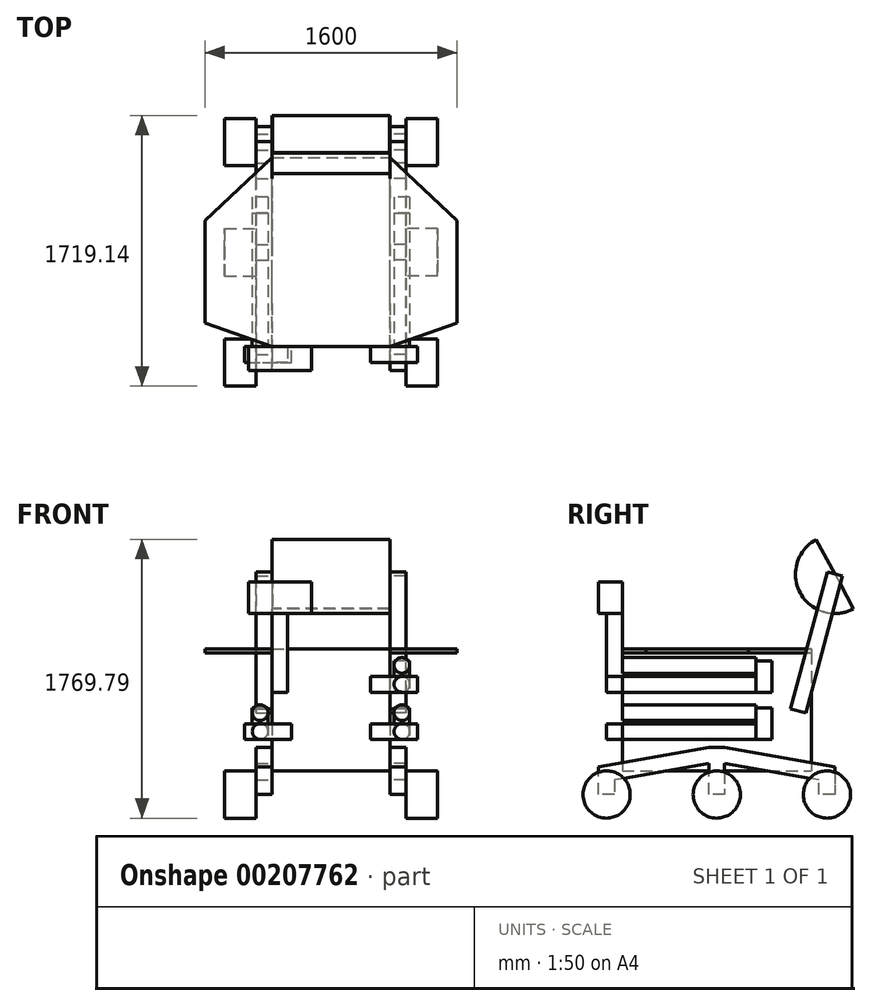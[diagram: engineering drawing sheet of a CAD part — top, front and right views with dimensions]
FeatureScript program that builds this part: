
annotation { "Feature Type Name" : "Feature", "Feature Type Description" : "" }
export const myFeature = defineFeature(function(context is Context, id is Id, definition is map)
    precondition{}
    {
        {
            var Q0;
            Q0=qCreatedBy(makeId("Front.planeOp"),FACE);
            var sketch = newSketch(context, id + "F0", { "sketchPlane" : qUnion([Q0])});
            skLineSegment(sketch, "E0.bottom", {"start": v(-375, 900) * mm, "end": v(375, 900) * mm});
            skLineSegment(sketch, "E0.top", {"start": v(-375, 150) * mm, "end": v(375, 150) * mm});
            skLineSegment(sketch, "E0.left", {"start": v(-375, 900) * mm, "end": v(-375, 150) * mm});
            skLineSegment(sketch, "E0.right", {"start": v(375, 900) * mm, "end": v(375, 150) * mm});
            skSolve(sketch);
        }
        {
            var Q0;
            Q0=makeQuery(id+"F0.imprint","IMPRINT",FACE,{"disambiguationData":[TD([[makeQuery(id+"F0.imprint","IMPRINT",EDGE,{"derivedFrom":sQuery(id+"F0.wireOp",EDGE,"E0.bottom")}),-1.0]])]});
            extrude(context, id + "F1", {"entities" : qUnion([Q0]), "endBound" : BoundingType.SYMMETRIC, "depth" : 1200 * mm, "offsetDistance" : 25 * mm});
        }
        {
            var Q0;
            Q0=makeQuery(id+"F1.opExtrude","SWEPT_FACE",FACE,{"disambiguationData":[OSD([sQuery(id+"F0.wireOp",EDGE,"E0.bottom")])]});
            var sketch = newSketch(context, id + "F2", { "sketchPlane" : qUnion([Q0])});
            skLineSegment(sketch, "E1", {"start": v(-375, -600) * mm, "end": v(-800, -450) * mm});
            skLineSegment(sketch, "E2", {"start": v(-800, -450) * mm, "end": v(-800, 200) * mm});
            skLineSegment(sketch, "E3", {"start": v(-800, 200) * mm, "end": v(-375, 600) * mm});
            skLineSegment(sketch, "E4", {"start": v(-375, 600) * mm, "end": v(375, 600) * mm});
            skLineSegment(sketch, "E5", {"start": v(375, 600) * mm, "end": v(800, 200) * mm});
            skLineSegment(sketch, "E6", {"start": v(800, 200) * mm, "end": v(800, -450) * mm});
            skLineSegment(sketch, "E7", {"start": v(800, -450) * mm, "end": v(375, -600) * mm});
            skLineSegment(sketch, "E8", {"start": v(375, -600) * mm, "end": v(-375, -600) * mm});
            skSolve(sketch);
        }
        {
            var Q0;
            Q0 = qSketchRegion(id + "F2", true);
            extrude(context, id + "F3", {"entities" : qUnion([Q0]), "operationType" : NewBodyOperationType.ADD, "depth" : 25 * mm, "offsetDistance" : 25 * mm});
        }
        {
            var Q0;
            Q0=makeQuery(id+"F1.opExtrude","SWEPT_FACE",FACE,{"disambiguationData":[OSD([sQuery(id+"F0.wireOp",EDGE,"E0.left")])]});
            var sketch = newSketch(context, id + "F4", { "sketchPlane" : qUnion([Q0])});
            skLineSegment(sketch, "E9.bottom", {"start": v(600, 1150) * mm, "end": v(700, 1150) * mm});
            skLineSegment(sketch, "E9.top", {"start": v(600, 650) * mm, "end": v(700, 650) * mm});
            skLineSegment(sketch, "E9.left", {"start": v(600, 1150) * mm, "end": v(600, 650) * mm});
            skLineSegment(sketch, "E9.right", {"start": v(700, 1150) * mm, "end": v(700, 650) * mm});
            skSolve(sketch);
        }
        {
            var Q0;
            Q0 = qSketchRegion(id + "F4", true);
            extrude(context, id + "F5", {"entities" : qUnion([Q0]), "operationType" : NewBodyOperationType.ADD, "oppositeDirection" : true, "depth" : 100 * mm, "offsetDistance" : 25 * mm});
        }
        {
            var Q0;
            Q0=makeQuery(id+"F5.opExtrude","SWEPT_FACE",FACE,{"disambiguationData":[OSD([sQuery(id+"F4.wireOp",EDGE,"E9.left")])]});
            var sketch = newSketch(context, id + "F6", { "sketchPlane" : qUnion([Q0])});
            skPoint(sketch, "E10.oppositeSnap0", {"position": v(325, 1150) * mm});
            skLineSegment(sketch, "E10.bottom", {"start": v(125, 1350) * mm, "end": v(525, 1350) * mm});
            skLineSegment(sketch, "E10.top", {"start": v(125, 1150) * mm, "end": v(525, 1150) * mm});
            skLineSegment(sketch, "E10.left", {"start": v(125, 1350) * mm, "end": v(125, 1150) * mm});
            skLineSegment(sketch, "E10.right", {"start": v(525, 1350) * mm, "end": v(525, 1150) * mm});
            skSolve(sketch);
        }
        {
            var Q0;
            Q0 = qSketchRegion(id + "F6", true);
            extrude(context, id + "F7", {"entities" : qUnion([Q0]), "oppositeDirection" : true, "depth" : 150 * mm, "offsetDistance" : 25 * mm});
        }
        {
            var Q0;
            Q0=makeQuery(id+"F5.boolean.opBoolean","MERGE",FACE,{"derivedFrom":[makeQuery(id+"F1.opExtrude","SWEPT_FACE",FACE,{"disambiguationData":[OSD([sQuery(id+"F0.wireOp",EDGE,"E0.left")])]}),makeQuery(id+"F5.opExtrude","CAP_FACE",FACE,{"disambiguationData":[OSD([sQuery(id+"F4.wireOp",EDGE,"E9.bottom"),sQuery(id+"F4.wireOp",EDGE,"E9.top"),sQuery(id+"F4.wireOp",EDGE,"E9.left"),sQuery(id+"F4.wireOp",EDGE,"E9.right")])],"isStart":true})]});
            var sketch = newSketch(context, id + "F8", { "sketchPlane" : qUnion([Q0])});
            skLineSegment(sketch, "E11", {"start": v(-50, 300) * mm, "end": v(-750, 176.57) * mm});
            skLineSegment(sketch, "E12", {"start": v(-750, 176.57) * mm, "end": v(-750, 0) * mm});
            skLineSegment(sketch, "E13", {"start": v(-750, 0) * mm, "end": v(-650, 0) * mm});
            skLineSegment(sketch, "E14", {"start": v(-650, 0) * mm, "end": v(-650, 92.66) * mm});
            skLineSegment(sketch, "E15", {"start": v(-650, 92.66) * mm, "end": v(-50, 198.46) * mm});
            skLineSegment(sketch, "E16", {"start": v(-50, 198.46) * mm, "end": v(-50, 0) * mm});
            skLineSegment(sketch, "E17", {"start": v(-50, 0) * mm, "end": v(50, 0) * mm});
            skLineSegment(sketch, "E18", {"start": v(50, 0) * mm, "end": v(50, 198.46) * mm});
            skLineSegment(sketch, "E19", {"start": v(50, 198.46) * mm, "end": v(650, 92.66) * mm});
            skLineSegment(sketch, "E20", {"start": v(650, 92.66) * mm, "end": v(650, 0) * mm});
            skLineSegment(sketch, "E21", {"start": v(650, 0) * mm, "end": v(750, 0) * mm});
            skLineSegment(sketch, "E22", {"start": v(750, 0) * mm, "end": v(750, 176.57) * mm});
            skLineSegment(sketch, "E23", {"start": v(750, 176.57) * mm, "end": v(50, 300) * mm});
            skLineSegment(sketch, "E24", {"start": v(-50, 300) * mm, "end": v(50, 300) * mm});
            skSolve(sketch);
        }
        {
            var Q0;
            Q0=makeQuery(id+"F1.opExtrude","SWEPT_FACE",FACE,{"disambiguationData":[OSD([sQuery(id+"F0.wireOp",EDGE,"E0.right")])]});
            var sketch = newSketch(context, id + "F9", { "sketchPlane" : qUnion([Q0])});
            skLineSegment(sketch, "E25.0", {"start": v(-750, 0) * mm, "end": v(-750, 176.57) * mm});
            skPoint(sketch, "E26.0", {"position": v(-700, 0) * mm});
            skLineSegment(sketch, "E27.0", {"start": v(-650, 0) * mm, "end": v(-750, 0) * mm});
            skLineSegment(sketch, "E28.0", {"start": v(-650, 92.66) * mm, "end": v(-650, 0) * mm});
            skLineSegment(sketch, "E29.0", {"start": v(-50, 198.46) * mm, "end": v(-650, 92.66) * mm});
            skLineSegment(sketch, "E30.0", {"start": v(-750, 176.57) * mm, "end": v(-50, 300) * mm});
            skLineSegment(sketch, "E31.0", {"start": v(-50, 0) * mm, "end": v(-50, 198.46) * mm});
            skLineSegment(sketch, "E32.0", {"start": v(50, 0) * mm, "end": v(-50, 0) * mm});
            skLineSegment(sketch, "E33.0", {"start": v(50, 198.46) * mm, "end": v(50, 0) * mm});
            skLineSegment(sketch, "E34.0", {"start": v(50, 300) * mm, "end": v(-50, 300) * mm});
            skLineSegment(sketch, "E35.0", {"start": v(650, 92.66) * mm, "end": v(50, 198.46) * mm});
            skLineSegment(sketch, "E36.0", {"start": v(50, 300) * mm, "end": v(750, 176.57) * mm});
            skLineSegment(sketch, "E37.0", {"start": v(750, 176.57) * mm, "end": v(750, 0) * mm});
            skLineSegment(sketch, "E38.0", {"start": v(650, 0) * mm, "end": v(650, 92.66) * mm});
            skLineSegment(sketch, "E39.0", {"start": v(750, 0) * mm, "end": v(650, 0) * mm});
            skSolve(sketch);
        }
        {
            var Q0;
            Q0 = qSketchRegion(id + "F8", true);
            extrude(context, id + "F10", {"entities" : qUnion([Q0]), "operationType" : NewBodyOperationType.ADD, "depth" : 100 * mm, "offsetDistance" : 25 * mm});
        }
        {
            var Q0;
            Q0 = qSketchRegion(id + "F9", true);
            extrude(context, id + "F11", {"entities" : qUnion([Q0]), "operationType" : NewBodyOperationType.ADD, "depth" : 100 * mm, "offsetDistance" : 25 * mm});
        }
        {
            var Q0;
            Q0=makeQuery(id+"F11.opExtrude","CAP_FACE",FACE,{"disambiguationData":[OSD([sQuery(id+"F9.wireOp",EDGE,"E25.0"),sQuery(id+"F9.wireOp",EDGE,"E27.0"),sQuery(id+"F9.wireOp",EDGE,"E28.0"),sQuery(id+"F9.wireOp",EDGE,"E29.0"),sQuery(id+"F9.wireOp",EDGE,"E30.0"),sQuery(id+"F9.wireOp",EDGE,"E31.0"),sQuery(id+"F9.wireOp",EDGE,"E32.0"),sQuery(id+"F9.wireOp",EDGE,"E33.0"),sQuery(id+"F9.wireOp",EDGE,"E34.0"),sQuery(id+"F9.wireOp",EDGE,"E35.0"),sQuery(id+"F9.wireOp",EDGE,"E36.0"),sQuery(id+"F9.wireOp",EDGE,"E37.0"),sQuery(id+"F9.wireOp",EDGE,"E38.0"),sQuery(id+"F9.wireOp",EDGE,"E39.0")])],"isStart":false});
            var sketch = newSketch(context, id + "F12", { "sketchPlane" : qUnion([Q0])});
            skCircle(sketch, "E40", {"center": v(-700, 0) * mm, "radius": 150 * mm});
            skCircle(sketch, "E41", {"center": v(0, 0) * mm, "radius": 150 * mm});
            skCircle(sketch, "E42", {"center": v(700, 0) * mm, "radius": 150 * mm});
            skSolve(sketch);
        }
        {
            var Q0;
            Q0=makeQuery(id+"F10.opExtrude","CAP_FACE",FACE,{"disambiguationData":[OSD([sQuery(id+"F8.wireOp",EDGE,"E11"),sQuery(id+"F8.wireOp",EDGE,"E12"),sQuery(id+"F8.wireOp",EDGE,"E13"),sQuery(id+"F8.wireOp",EDGE,"E14"),sQuery(id+"F8.wireOp",EDGE,"E15"),sQuery(id+"F8.wireOp",EDGE,"E16"),sQuery(id+"F8.wireOp",EDGE,"E17"),sQuery(id+"F8.wireOp",EDGE,"E18"),sQuery(id+"F8.wireOp",EDGE,"E19"),sQuery(id+"F8.wireOp",EDGE,"E20"),sQuery(id+"F8.wireOp",EDGE,"E21"),sQuery(id+"F8.wireOp",EDGE,"E22"),sQuery(id+"F8.wireOp",EDGE,"E23"),sQuery(id+"F8.wireOp",EDGE,"E24")])],"isStart":false});
            var sketch = newSketch(context, id + "F13", { "sketchPlane" : qUnion([Q0])});
            skCircle(sketch, "E43.0", {"center": v(-700, 0) * mm, "radius": 150 * mm});
            skCircle(sketch, "E44.0", {"center": v(0, 0) * mm, "radius": 150 * mm});
            skCircle(sketch, "E45.0", {"center": v(700, 0) * mm, "radius": 150 * mm});
            skSolve(sketch);
        }
        {
            var Q0;
            Q0 = qSketchRegion(id + "F12", true);
            extrude(context, id + "F14", {"entities" : qUnion([Q0]), "operationType" : NewBodyOperationType.ADD, "depth" : 200 * mm, "offsetDistance" : 25 * mm});
        }
        {
            var Q0;
            Q0 = qSketchRegion(id + "F13", true);
            extrude(context, id + "F15", {"entities" : qUnion([Q0]), "operationType" : NewBodyOperationType.ADD, "depth" : 200 * mm, "offsetDistance" : 25 * mm});
        }
        {
            var Q0;
            Q0=qCreatedBy(makeId("Right.planeOp"),FACE);
            var sketch = newSketch(context, id + "F16", { "sketchPlane" : qUnion([Q0])});
            skLineSegment(sketch, "E46", {"start": v(630.86, 1619.79) * mm, "end": v(869.14, 1180.21) * mm});
            skArc(sketch, "E47", {"start": v(869.14, 1180.21) * mm, "mid": v(530.21, 1280.86) * mm, "end": v(630.86, 1619.79) * mm});
            skSolve(sketch);
        }
        {
            var Q0;
            Q0=makeQuery(id+"F16.imprint","IMPRINT",FACE,{"disambiguationData":[TD([[makeQuery(id+"F16.imprint","IMPRINT",EDGE,{"derivedFrom":sQuery(id+"F16.wireOp",EDGE,"E46")}),-1.0]])]});
            extrude(context, id + "F17", {"entities" : qUnion([Q0]), "endBound" : BoundingType.SYMMETRIC, "depth" : 750 * mm, "offsetDistance" : 25 * mm});
        }
        {
            var Q0;
            Q0=makeQuery(id+"F17.opExtrude","SWEPT_FACE",FACE,{"disambiguationData":[OSD([sQuery(id+"F16.wireOp",EDGE,"E46")])]});
            var Q1;
            Q1=makeQuery(id+"F17.opExtrude","SWEPT_BODY",BODY,{"disambiguationData":[OSD([sQuery(id+"F16.wireOp",EDGE,"E46"),sQuery(id+"F16.wireOp",EDGE,"E47")])]});
            shell(context, id + "F18", {"entities" : qUnion([Q0]), "parts" : qUnion([Q1]), "thickness" : 3 * mm});
        }
        {
            var Q0;
            {var subQ0=sQuery(id+"F4.wireOp",EDGE,"E9.top");var subQ2=sQuery(id+"F4.wireOp",EDGE,"E9.bottom");var subQ9=sQuery(id+"F2.wireOp",EDGE,"E1");var subQ12=sQuery(id+"F0.wireOp",EDGE,"E0.left");var subQ15=sQuery(id+"F4.wireOp",EDGE,"E9.left");var subQ16=sQuery(id+"F4.wireOp",EDGE,"E9.right");Q0=makeQuery(id+"F10.boolean.opBoolean","SPLIT",FACE,{"disambiguationData":[TD([makeQuery(id+"F3.opExtrude","SWEPT_FACE",FACE,{"disambiguationData":[OSD([subQ9])]})])],"derivedFrom":makeQuery(id+"F5.boolean.opBoolean","MERGE",FACE,{"derivedFrom":[makeQuery(id+"F1.opExtrude","SWEPT_FACE",FACE,{"disambiguationData":[OSD([subQ12])]}),makeQuery(id+"F5.opExtrude","CAP_FACE",FACE,{"disambiguationData":[OSD([subQ2,subQ0,subQ15,subQ16])],"isStart":true})]})});}
            var sketch = newSketch(context, id + "F19", { "sketchPlane" : qUnion([Q0])});
            skLineSegment(sketch, "E48", {"start": v(-701.7, 1412.94) * mm, "end": v(-798.3, 1387.06) * mm});
            skLineSegment(sketch, "E49", {"start": v(-798.3, 1387.06) * mm, "end": v(-565.36, 517.73) * mm});
            skLineSegment(sketch, "E50", {"start": v(-565.36, 517.73) * mm, "end": v(-468.77, 543.6) * mm});
            skLineSegment(sketch, "E51", {"start": v(-468.77, 543.6) * mm, "end": v(-701.7, 1412.94) * mm});
            skSolve(sketch);
        }
        {
            var Q0;
            {var subQ5=sQuery(id+"F2.wireOp",EDGE,"E5");var subQ6=sQuery(id+"F0.wireOp",EDGE,"E0.right");Q0=makeQuery(id+"F11.boolean.opBoolean","SPLIT",FACE,{"disambiguationData":[TD([makeQuery(id+"F3.opExtrude","SWEPT_FACE",FACE,{"disambiguationData":[OSD([subQ5])]})])],"derivedFrom":makeQuery(id+"F1.opExtrude","SWEPT_FACE",FACE,{"disambiguationData":[OSD([subQ6])]})});}
            var sketch = newSketch(context, id + "F20", { "sketchPlane" : qUnion([Q0])});
            skLineSegment(sketch, "E52.0", {"start": v(468.77, 543.6) * mm, "end": v(701.7, 1412.94) * mm});
            skLineSegment(sketch, "E53.0", {"start": v(565.36, 517.73) * mm, "end": v(468.77, 543.6) * mm});
            skLineSegment(sketch, "E54.0", {"start": v(798.3, 1387.06) * mm, "end": v(565.36, 517.73) * mm});
            skLineSegment(sketch, "E55.0", {"start": v(701.7, 1412.94) * mm, "end": v(798.3, 1387.06) * mm});
            skSolve(sketch);
        }
        {
            var Q0;
            Q0 = qSketchRegion(id + "F19", true);
            extrude(context, id + "F21", {"entities" : qUnion([Q0]), "depth" : 100 * mm, "offsetDistance" : 25 * mm});
        }
        {
            var Q0;
            Q0 = qSketchRegion(id + "F20", true);
            extrude(context, id + "F22", {"entities" : qUnion([Q0]), "depth" : 100 * mm, "offsetDistance" : 25 * mm});
        }
        {
            var Q0;
            Q0=makeQuery(id+"F3.boolean.opBoolean","MERGE",FACE,{"derivedFrom":[makeQuery(id+"F1.opExtrude","CAP_FACE",FACE,{"disambiguationData":[OSD([sQuery(id+"F0.wireOp",EDGE,"E0.bottom"),sQuery(id+"F0.wireOp",EDGE,"E0.top"),sQuery(id+"F0.wireOp",EDGE,"E0.left"),sQuery(id+"F0.wireOp",EDGE,"E0.right")])],"isStart":false}),makeQuery(id+"F3.opExtrude","SWEPT_FACE",FACE,{"disambiguationData":[OSD([sQuery(id+"F2.wireOp",EDGE,"E8")])]})]});
            var sketch = newSketch(context, id + "F23", { "sketchPlane" : qUnion([Q0])});
            skCircle(sketch, "E56", {"center": v(450, 820) * mm, "radius": 50 * mm});
            skCircle(sketch, "E57", {"center": v(450, 700) * mm, "radius": 50 * mm});
            skCircle(sketch, "E58", {"center": v(450, 520) * mm, "radius": 50 * mm});
            skCircle(sketch, "E59", {"center": v(450, 400) * mm, "radius": 50 * mm});
            skCircle(sketch, "E60", {"center": v(-450, 520) * mm, "radius": 50 * mm});
            skCircle(sketch, "E61", {"center": v(-450, 400) * mm, "radius": 50 * mm});
            skSolve(sketch);
        }
        {
            var Q0;
            Q0 = qSketchRegion(id + "F23", true);
            extrude(context, id + "F24", {"entities" : qUnion([Q0]), "operationType" : NewBodyOperationType.ADD, "oppositeDirection" : true, "depth" : 850 * mm, "offsetDistance" : 25 * mm});
        }
        {
            var Q0;
            Q0=makeQuery(id+"F3.boolean.opBoolean","MERGE",FACE,{"derivedFrom":[makeQuery(id+"F1.opExtrude","CAP_FACE",FACE,{"disambiguationData":[OSD([sQuery(id+"F0.wireOp",EDGE,"E0.bottom"),sQuery(id+"F0.wireOp",EDGE,"E0.top"),sQuery(id+"F0.wireOp",EDGE,"E0.left"),sQuery(id+"F0.wireOp",EDGE,"E0.right")])],"isStart":false}),makeQuery(id+"F3.opExtrude","SWEPT_FACE",FACE,{"disambiguationData":[OSD([sQuery(id+"F2.wireOp",EDGE,"E8")])]})]});
            var sketch = newSketch(context, id + "F25", { "sketchPlane" : qUnion([Q0])});
            skLineSegment(sketch, "E62.bottom", {"start": v(-550, 450) * mm, "end": v(-250, 450) * mm});
            skLineSegment(sketch, "E62.top", {"start": v(-550, 350) * mm, "end": v(-250, 350) * mm});
            skLineSegment(sketch, "E62.left", {"start": v(-550, 450) * mm, "end": v(-550, 350) * mm});
            skLineSegment(sketch, "E62.right", {"start": v(-250, 450) * mm, "end": v(-250, 350) * mm});
            skLineSegment(sketch, "E63.bottom", {"start": v(250, 450) * mm, "end": v(550, 450) * mm});
            skLineSegment(sketch, "E63.top", {"start": v(250, 350) * mm, "end": v(550, 350) * mm});
            skLineSegment(sketch, "E63.left", {"start": v(250, 450) * mm, "end": v(250, 350) * mm});
            skLineSegment(sketch, "E63.right", {"start": v(550, 450) * mm, "end": v(550, 350) * mm});
            skLineSegment(sketch, "E64.bottom", {"start": v(250, 750) * mm, "end": v(550, 750) * mm});
            skLineSegment(sketch, "E64.top", {"start": v(250, 650) * mm, "end": v(550, 650) * mm});
            skLineSegment(sketch, "E64.left", {"start": v(250, 750) * mm, "end": v(250, 650) * mm});
            skLineSegment(sketch, "E64.right", {"start": v(550, 750) * mm, "end": v(550, 650) * mm});
            skSolve(sketch);
        }
        {
            var Q0;
            Q0 = qSketchRegion(id + "F25", true);
            extrude(context, id + "F26", {"entities" : qUnion([Q0]), "depth" : 100 * mm, "offsetDistance" : 25 * mm});
        }
        {
            var Q0;
            Q0=makeQuery(id+"F1.opExtrude","SWEPT_BODY",BODY,{"disambiguationData":[OSD([sQuery(id+"F0.wireOp",EDGE,"E0.bottom"),sQuery(id+"F0.wireOp",EDGE,"E0.top"),sQuery(id+"F0.wireOp",EDGE,"E0.left"),sQuery(id+"F0.wireOp",EDGE,"E0.right")])]});
            var Q1;
            Q1=makeQuery(id+"F26.opExtrude","SWEPT_BODY",BODY,{"disambiguationData":[OSD([sQuery(id+"F25.wireOp",EDGE,"E62.bottom"),sQuery(id+"F25.wireOp",EDGE,"E62.top"),sQuery(id+"F25.wireOp",EDGE,"E62.left"),sQuery(id+"F25.wireOp",EDGE,"E62.right")])]});
            booleanBodies(context, id + "F27", {"operationType" : BooleanOperationType.UNION, "tools" : qUnion([Q0, Q1])});
        }
        {
            var Q0;
            Q0=makeQuery(id+"F1.opExtrude","SWEPT_BODY",BODY,{"disambiguationData":[OSD([sQuery(id+"F0.wireOp",EDGE,"E0.bottom"),sQuery(id+"F0.wireOp",EDGE,"E0.top"),sQuery(id+"F0.wireOp",EDGE,"E0.left"),sQuery(id+"F0.wireOp",EDGE,"E0.right")])]});
            var Q1;
            Q1=makeQuery(id+"F26.opExtrude","SWEPT_BODY",BODY,{"disambiguationData":[OSD([sQuery(id+"F25.wireOp",EDGE,"E64.bottom"),sQuery(id+"F25.wireOp",EDGE,"E64.top"),sQuery(id+"F25.wireOp",EDGE,"E64.left"),sQuery(id+"F25.wireOp",EDGE,"E64.right")])]});
            booleanBodies(context, id + "F28", {"operationType" : BooleanOperationType.UNION, "tools" : qUnion([Q0, Q1])});
        }
        {
            var Q0;
            Q0=makeQuery(id+"F1.opExtrude","SWEPT_BODY",BODY,{"disambiguationData":[OSD([sQuery(id+"F0.wireOp",EDGE,"E0.bottom"),sQuery(id+"F0.wireOp",EDGE,"E0.top"),sQuery(id+"F0.wireOp",EDGE,"E0.left"),sQuery(id+"F0.wireOp",EDGE,"E0.right")])]});
            var Q1;
            Q1=makeQuery(id+"F26.opExtrude","SWEPT_BODY",BODY,{"disambiguationData":[OSD([sQuery(id+"F25.wireOp",EDGE,"E63.bottom"),sQuery(id+"F25.wireOp",EDGE,"E63.top"),sQuery(id+"F25.wireOp",EDGE,"E63.left"),sQuery(id+"F25.wireOp",EDGE,"E63.right")])]});
            booleanBodies(context, id + "F29", {"operationType" : BooleanOperationType.UNION, "tools" : qUnion([Q0, Q1])});
        }
        {
            var Q0;
            Q0=makeQuery(id+"F24.opExtrude","CAP_FACE",FACE,{"disambiguationData":[OSD([sQuery(id+"F23.wireOp",EDGE,"E59")])],"isStart":false});
            var sketch = newSketch(context, id + "F30", { "sketchPlane" : qUnion([Q0])});
            skLineSegment(sketch, "E65.bottom", {"start": v(-500, 550) * mm, "end": v(-400, 550) * mm});
            skLineSegment(sketch, "E65.top", {"start": v(-500, 350) * mm, "end": v(-400, 350) * mm});
            skLineSegment(sketch, "E65.left", {"start": v(-500, 550) * mm, "end": v(-500, 350) * mm});
            skLineSegment(sketch, "E65.right", {"start": v(-400, 550) * mm, "end": v(-400, 350) * mm});
            skLineSegment(sketch, "E66.bottom", {"start": v(400, 550) * mm, "end": v(500, 550) * mm});
            skLineSegment(sketch, "E66.top", {"start": v(400, 350) * mm, "end": v(500, 350) * mm});
            skLineSegment(sketch, "E66.left", {"start": v(400, 550) * mm, "end": v(400, 350) * mm});
            skLineSegment(sketch, "E66.right", {"start": v(500, 550) * mm, "end": v(500, 350) * mm});
            skLineSegment(sketch, "E67.bottom", {"start": v(-500, 850) * mm, "end": v(-400, 850) * mm});
            skLineSegment(sketch, "E67.top", {"start": v(-500, 650) * mm, "end": v(-400, 650) * mm});
            skLineSegment(sketch, "E67.left", {"start": v(-500, 850) * mm, "end": v(-500, 650) * mm});
            skLineSegment(sketch, "E67.right", {"start": v(-400, 850) * mm, "end": v(-400, 650) * mm});
            skSolve(sketch);
        }
        {
            var Q0;
            Q0 = qSketchRegion(id + "F30", true);
            extrude(context, id + "F31", {"entities" : qUnion([Q0]), "depth" : 100 * mm, "offsetDistance" : 25 * mm});
        }
    });
